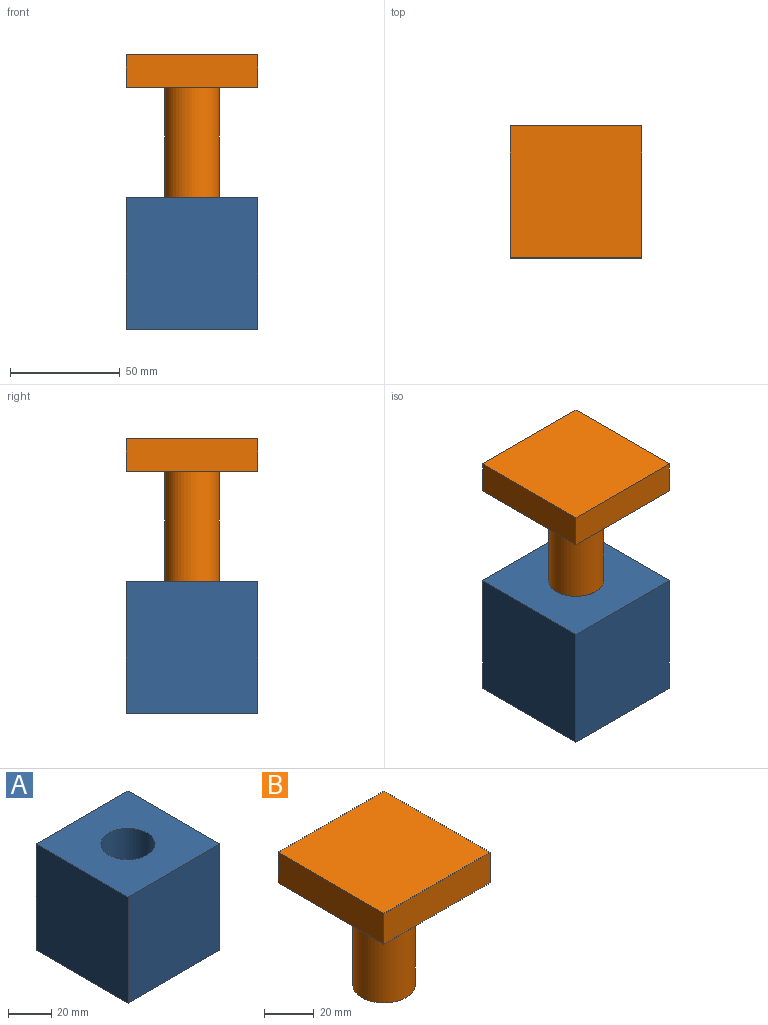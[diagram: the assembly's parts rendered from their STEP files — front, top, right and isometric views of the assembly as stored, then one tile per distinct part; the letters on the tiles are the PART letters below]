
ASSEMBLY  parts=2 mates=1
PART A: 8 faces, bbox 60x60x60 mm
  f0: plane 60x60mm, normal (0,1,0), area 3600mm2, adj f1,f3,f4,f5
  f1: plane 60x60mm, normal (-1,0,0), area 3600mm2, adj f0,f2,f4,f5
  f2: plane 60x60mm, normal (0,-1,0), area 3600mm2, adj f1,f3,f4,f5
  f3: plane 60x60mm, normal (1,0,0), area 3600mm2, adj f0,f2,f4,f5
  f4: plane 60x60mm, normal (0,0,1), area 3109.1mm2, adj f0,f1,f2,f3,f6
  f5: plane 60x60mm, normal (0,0,-1), area 3600mm2, adj f0,f1,f2,f3
  f6: cylinder r=12.5mm len=50mm, axis (0,0,1), area 3927mm2, adj f4,f7
  f7: plane 25x25mm, normal (0,0,1), area 490.9mm2, adj f6
PART B: 8 faces, bbox 60x60x65 mm
  f0: plane 60x15mm, normal (0,1,0), area 900mm2, adj f1,f3,f4,f5
  f1: plane 60x15mm, normal (-1,0,0), area 900mm2, adj f0,f2,f4,f5
  f2: plane 60x15mm, normal (0,-1,0), area 900mm2, adj f1,f3,f4,f5
  f3: plane 60x15mm, normal (1,0,0), area 900mm2, adj f0,f2,f4,f5
  f4: plane 60x60mm, normal (0,0,1), area 3600mm2, adj f0,f1,f2,f3
  f5: plane 60x60mm, normal (0,0,-1), area 3109.1mm2, adj f0,f1,f2,f3,f6
  f6: cylinder r=12.5mm len=50mm, axis (0,0,1), area 3927mm2, adj f5,f7
  f7: plane 25x25mm, normal (0,0,-1), area 490.9mm2, adj f6
PLACE A t=(-81.94,27.63,86.21)mm
PLACE B rot(axis=(0,0,1),90deg) t=(-81.94,-32.37,86.21)mm
MATE slider B.f6 <-> A.f6  axis (0,0,1) through (-51.94,-2.37,146.21)mm
